# Revit family: Valve-Pressure_Relief-Cla_Val-55L_60-FNPT--
name_source: partatom
category: Pipe Accessories
units: mm (PartAtom-declared; Revit-internal decimal feet)

## family parameters
Always vertical = Yes
Cut with Voids When Loaded = No
OmniClass Number = 23.65.55.00
OmniClass Title = Distribution of Supplied Liquids/Gases
Part Type = Valve - Breaks Into
Round Connector Dimension = Use Radius
Shared = No
Work Plane-Based = No

## types (1)
- ERROR_LOAD TYPE CATALOG
    Assembly Code = D2090900
    Bottom Plug Material = Metal - Cla-Val - Stainless Steel
    Cap Height = 2.25 "
    Cap Material = Plastic - Cla-Val - Red
    Cap Mount Height = 0.172 "
    Cap Mount Radius = 0.444 "
    Cap Radius = 0.4 "
    Connection Axis to Lower Flange = 1.31 "
    Connection Axis to Valve Bottom = 1.31 "
    Connection Axis to Valve Top = 6.75 "
    Connection Radius = 0"
    Connection Size = 1"
    Connection Type = Female Thread
    Connection to Connection = 2.433 "
    Cover Bevel Radius = 0.25 "
    Cover Radius = 0.667 "
    Cv Coefficient = 6
    Default Elevation = 0 "
    Description = Pressure Relief Valve
    ENGworks URL = http://www.ENGworksGlobal.com
    Flow Configuration = In/Out
    K Coefficient = 1.545771
    K Coefficient Table = Globe Valve Threaded
    Lock Nut Circumscribe Length = 0.889 "
    Lock Nut Height = 0.575 "
    Loss Method = K Coefficient
    Lower Flange Height = 0.233 "
    Manufacturer = Cla_Val
    Maximum Flow Rate = 25 GPM
    Maximum Flow Rate Value = 25
    Maximum Operating Temperature = 180 °F
    Maximum Working Pressure = 400.00 psi
    Minimum Flow Rate = 0 GPM
    Minimum Flow Rate Value = 0
    Minimum Operating Temperature = 0 °F
    Model = 55L-60
    Nut Union Circumscribe Length = 1.232 "
    Overall Height = 8.62 "
    Plug Mount Radius = 0.5 "
    Pressure Gauge Port Outside Diameter = 0.405 "
    Pressure Gauge Port Outside Radius = 0.203 "
    Product Page URL = https://www.cla-val.com
    Series = Pressure Relief Valves
    Standards = UL Listed and FM Approved
    Threaded Female End Insertion Depth = 0.534 "
    Threaded Female End Inside Diameter = 0.7 "
    Threaded Female End Inside Radius = 0.35 "
    Threaded Female End Outside Radius = 0.467 "
    Tick Size = 1.404 "
    URL = https://www.cla-val.com
    Unit Weight = 0.00 lb
    Unit Weight Value = 0
    Upper Flange Height = 0.233 "
    Valve Body Diameter = 2 "
    Valve Body Material = Metal - Cla-Val - Bronze
    Valve Body Radius = 1 "
    Valve Flange Outside Diameter = 3.12 "
    Valve Flange Outside Radius = 1.56 "
    Valve Length = 3.5 "
    Valve Main Body Plug Circumscribe Length = 0.695 "
    Valve Plug Nut Height = 0.562 "
    Valve Plug Nut Width = 0.588 "
    Version = 1

## geometry (parser evidence)
native form markers: Sweep x3
no freeform markers — native parametric forms only
